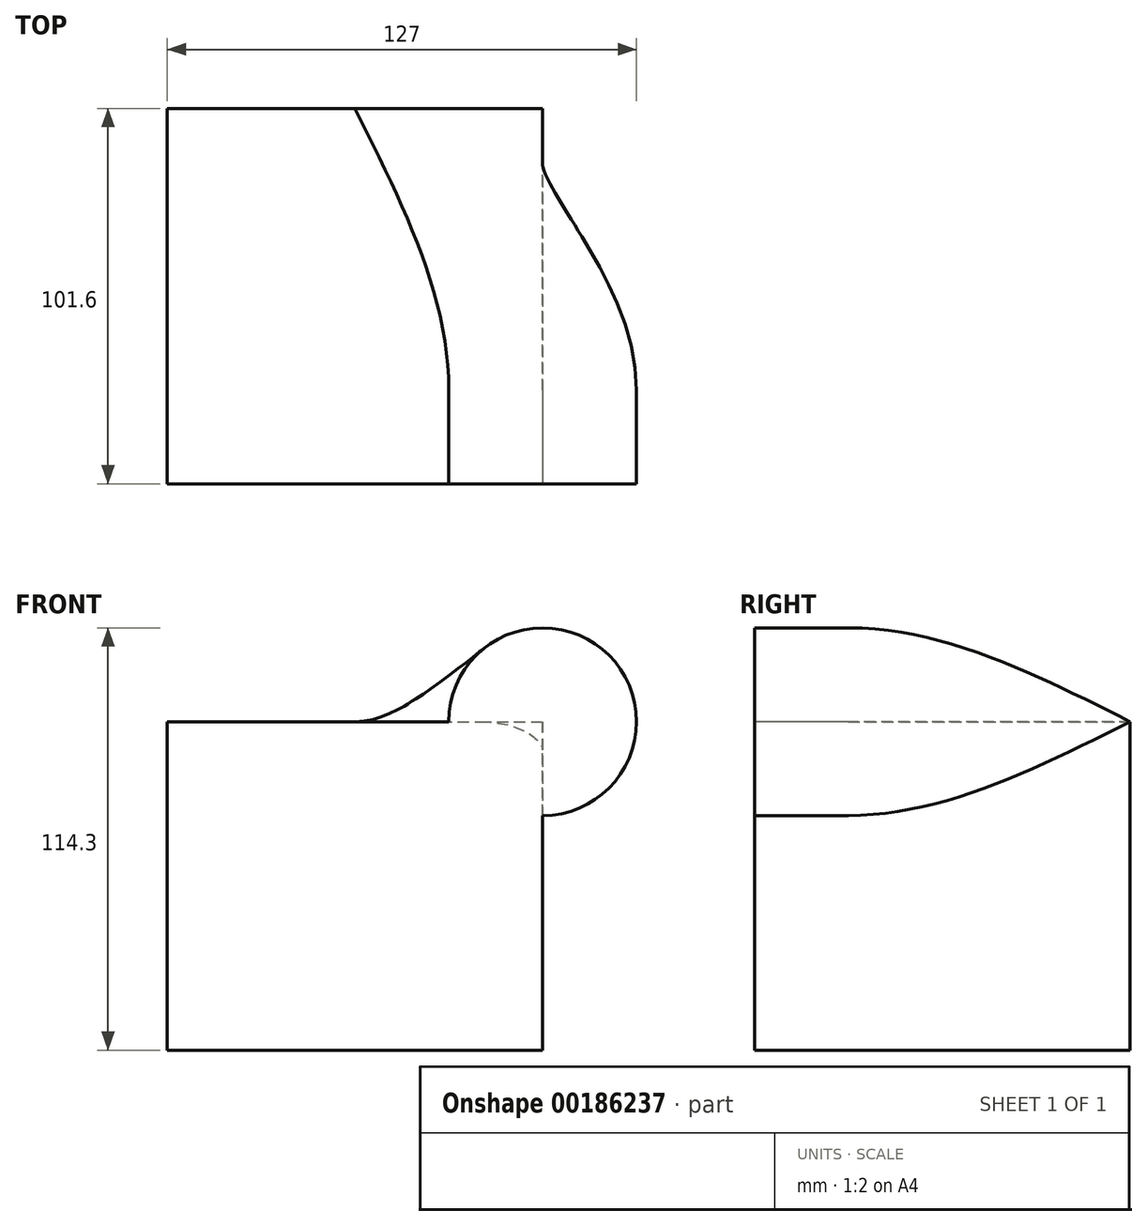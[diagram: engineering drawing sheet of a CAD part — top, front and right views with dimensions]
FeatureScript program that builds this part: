
annotation { "Feature Type Name" : "Feature", "Feature Type Description" : "" }
export const myFeature = defineFeature(function(context is Context, id is Id, definition is map)
    precondition{}
    {
        {
            var Q0;
            Q0=qCreatedBy(makeId("Front.planeOp"),FACE);
            var sketch = newSketch(context, id + "F0", { "sketchPlane" : qUnion([Q0])});
            skLineSegment(sketch, "E0.bottom", {"start": v(-50.8, -44.45) * mm, "end": v(50.8, -44.45) * mm});
            skLineSegment(sketch, "E0.top", {"start": v(-50.8, 44.45) * mm, "end": v(25.4, 44.45) * mm});
            skLineSegment(sketch, "E0.left", {"start": v(-50.8, -44.45) * mm, "end": v(-50.8, 44.45) * mm});
            skLineSegment(sketch, "E0.right", {"start": v(50.8, -44.45) * mm, "end": v(50.8, 19.05) * mm});
            skArc(sketch, "E1", {"start": v(50.8, 19.05) * mm, "mid": v(68.76, 62.41) * mm, "end": v(25.4, 44.45) * mm});
            skSolve(sketch);
        }
        {
            var Q0;
            Q0=makeQuery(id+"F0.imprint","IMPRINT",FACE,{"disambiguationData":[TD([[makeQuery(id+"F0.imprint","IMPRINT",EDGE,{"derivedFrom":sQuery(id+"F0.wireOp",EDGE,"E0.bottom")}),1.0]])]});
            extrude(context, id + "F1", {"entities" : qUnion([Q0]), "oppositeDirection" : true, "depth" : 25.4 * mm});
        }
        {
            var Q0;
            Q0=qCreatedBy(makeId("Front.planeOp"),FACE);
            cPlane(context, id + "F2", {"entities" : qUnion([Q0]), "cplaneType" : CPlaneType.OFFSET, "offset" : 101.6 * mm, "oppositeDirection" : true, "width" : 152.4 * mm, "height" : 152.4 * mm});
        }
        {
            var Q0;
            Q0=qCreatedBy(id+"F2.planeOp",FACE);
            var sketch = newSketch(context, id + "F3", { "sketchPlane" : qUnion([Q0])});
            skLineSegment(sketch, "E2.bottom", {"start": v(-50.8, 44.45) * mm, "end": v(50.8, 44.45) * mm});
            skLineSegment(sketch, "E2.top", {"start": v(-50.8, -44.45) * mm, "end": v(50.8, -44.45) * mm});
            skLineSegment(sketch, "E2.left", {"start": v(-50.8, 44.45) * mm, "end": v(-50.8, -44.45) * mm});
            skLineSegment(sketch, "E2.right", {"start": v(50.8, 44.45) * mm, "end": v(50.8, -44.45) * mm});
            skSolve(sketch);
        }
        {
            var Q1;
            Q1=makeQuery(id+"F1.opExtrude","CAP_FACE",FACE,{"disambiguationData":[OSD([sQuery(id+"F0.wireOp",EDGE,"E0.bottom"),sQuery(id+"F0.wireOp",EDGE,"E0.top"),sQuery(id+"F0.wireOp",EDGE,"E0.left"),sQuery(id+"F0.wireOp",EDGE,"E0.right"),sQuery(id+"F0.wireOp",EDGE,"E1")])],"isStart":false});
            var Q2;
            Q2=makeQuery(id+"F3.imprint","IMPRINT",FACE,{"disambiguationData":[TD([[makeQuery(id+"F3.imprint","IMPRINT",EDGE,{"derivedFrom":sQuery(id+"F3.wireOp",EDGE,"E2.bottom")}),-1.0]])]});
            var Q3;
            Q3=makeQuery(id+"F1.opExtrude","CAP_VERTEX",VERTEX,{"disambiguationData":[OSD([sQuery(id+"F0.wireOp",EDGE,"E0.top"),sQuery(id+"F0.wireOp",EDGE,"E0.left")])],"isStart":false});
            var Q4;
            Q4=sQuery(id+"F3.wireOp",VERTEX,"E2.bottom.start");
            loft(context, id + "F4", {"operationType" : NewBodyOperationType.ADD, "startCondition" : LoftEndDerivativeType.NORMAL_TO_PROFILE, "startMagnitude" : 1, "sheetProfilesArray" : [{ "sheetProfileEntities" : qUnion([Q1]) }, { "sheetProfileEntities" : qUnion([Q2]) }], "matchConnections" : true, "connections" : [{ "connectionEntities" : qUnion([Q3, Q4]), "connectionEdgeQueries" : qUnion([]), "connectionEdgeParameters" : [] }]});
        }
    });
